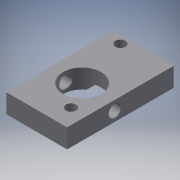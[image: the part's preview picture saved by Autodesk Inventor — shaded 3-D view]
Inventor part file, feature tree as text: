
AUTODESK INVENTOR PART (.ipt)
format: ipt  version: 2016 (Build 200138000, 138)  size: 175,104 bytes
history: native  units: mm
features: extrude x7, sketch x6, projected_geometry x4
ambient origin geometry x8: Origin, YZ Plane, XZ Plane, XY Plane, X Axis, Y Axis, Z Axis, Center Point
bodies: Solid1 (feature_tree)
feature tree (17):
  extrude  "Extrusion1"  Depth=28.0mm
  extrude  "Extrusion3"  Depth=5.0mm
  extrude  "Extrusion4"  Depth=1.5mm TaperAngle=0.0deg
  extrude  "Extrusion5"  Depth=10.0mm
  extrude  "Extrusion6"  Depth=1.5mm
  extrude  "Extrusion8"  Depth=10.0mm
  extrude  "Extrusion9"  Depth=1.5mm TaperAngle=0.0deg
  sketch  "Sketch4"  dims[d0=17.0mm d1=28.0mm]
  projected_geometry  "Projected Loop2"
  sketch  "Sketch5"  dims[d5=5.0mm d6=0.0mm d15=6.0mm]
  projected_geometry  "Projected Loop3"
  sketch  "Sketch6"  dims[d17=5.5mm d18=1.5mm d19=0.0mm]
  projected_geometry  "Projected Loop4"
  sketch  "Sketch7"  dims[d20=10.0mm d21=12.047087mm]
  sketch  "Sketch8"  dims[d22=1.5mm d23=0.0mm d24=2.7mm]
  sketch  "Sketch9"  dims[d25=4.5mm d26=2.0mm d27=1.5mm d28=0.0mm d30=20.0mm d31=4.0mm d32=2.7mm d33=4.5mm d34=5.0mm d35=1.5mm d36=0.0mm d37=3.2mm d41=12.5mm d42=10.0mm d43=0.0mm d44=10.0mm d45=0.0mm d47=0.5mm d48=0.5mm d49=2.5mm]
  projected_geometry  "Projected Loop6"
